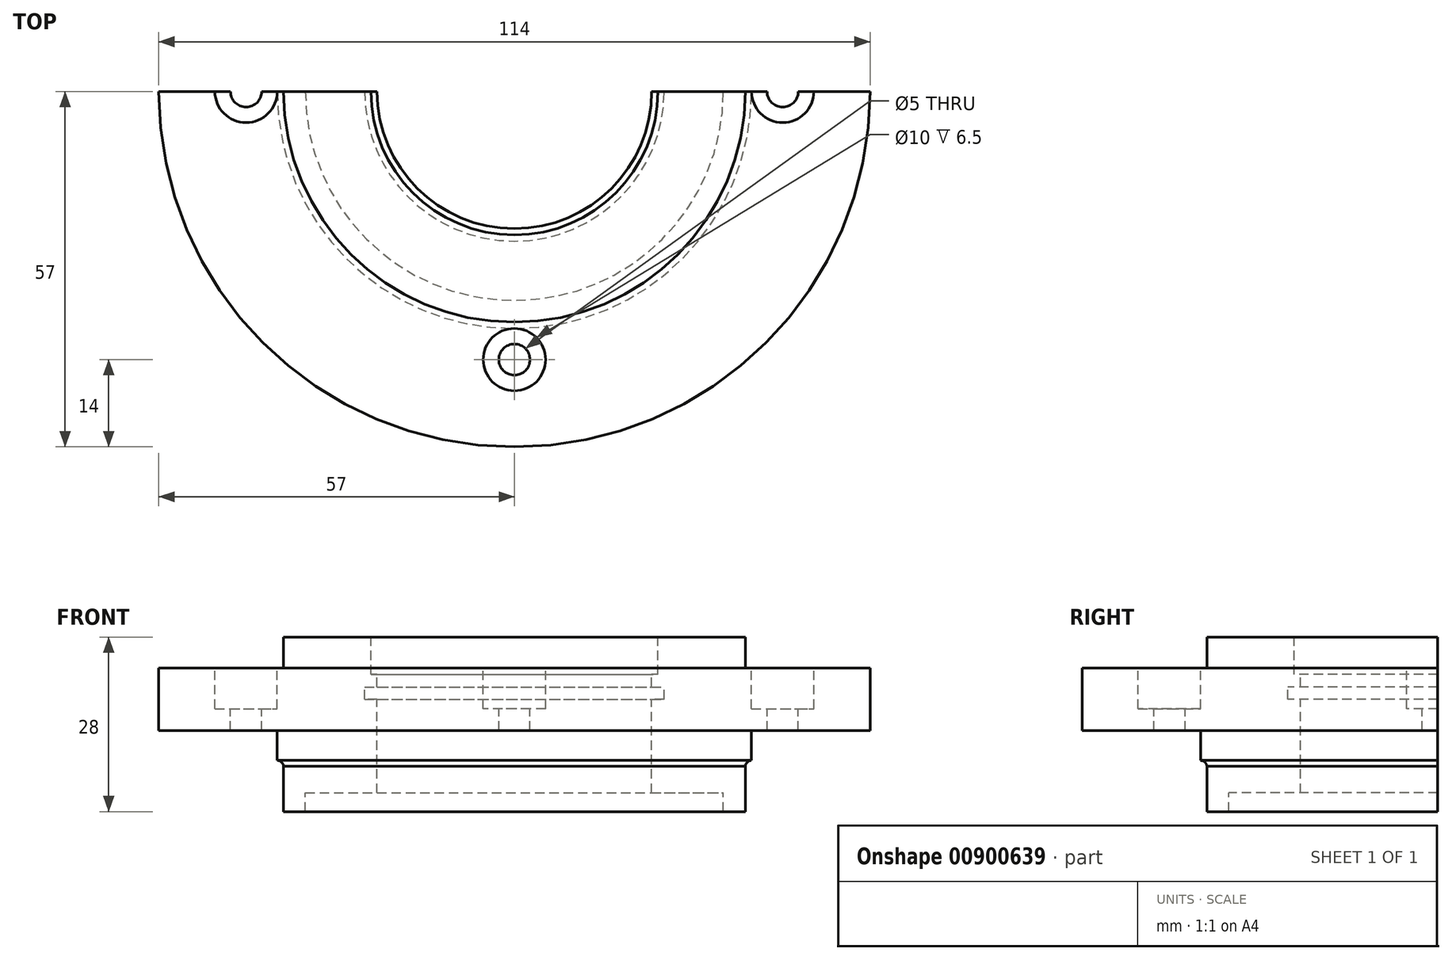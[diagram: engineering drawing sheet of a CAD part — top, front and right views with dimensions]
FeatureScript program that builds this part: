
annotation { "Feature Type Name" : "Feature", "Feature Type Description" : "" }
export const myFeature = defineFeature(function(context is Context, id is Id, definition is map)
    precondition{}
    {
        {
            var Q0;
            Q0=qCreatedBy(makeId("Front.planeOp"),FACE);
            var sketch = newSketch(context, id + "F0", { "sketchPlane" : qUnion([Q0])});
            skLineSegment(sketch, "E0.bottom", {"start": v(5, 21.92) * mm, "end": v(19, 21.92) * mm});
            skLineSegment(sketch, "E0.top", {"start": v(5, -6.08) * mm, "end": v(8.5, -6.08) * mm});
            skLineSegment(sketch, "E0.left", {"start": v(-15, 16.92) * mm, "end": v(-15, 6.92) * mm});
            skLineSegment(sketch, "E0.right", {"start": v(20, 15.92) * mm, "end": v(20, 13.92) * mm});
            skLineSegment(sketch, "E1", {"start": v(5, 21.92) * mm, "end": v(5, 16.92) * mm});
            skLineSegment(sketch, "E2", {"start": v(5, 16.92) * mm, "end": v(-15, 16.92) * mm});
            skLineSegment(sketch, "E3", {"start": v(-15, 6.92) * mm, "end": v(4, 6.92) * mm});
            skLineSegment(sketch, "E4", {"start": v(4, 6.92) * mm, "end": v(4, 2.12) * mm});
            skLineSegment(sketch, "E5", {"start": v(5, 1.2) * mm, "end": v(5, -6.08) * mm});
            skArc(sketch, "E6", {"start": v(5, 1.2) * mm, "mid": v(4.68, 1.86) * mm, "end": v(4, 2.12) * mm});
            skLineSegment(sketch, "E7", {"start": v(19, 21.92) * mm, "end": v(19, 15.92) * mm});
            skLineSegment(sketch, "E8", {"start": v(19, 15.92) * mm, "end": v(20, 15.92) * mm});
            skLineSegment(sketch, "E9", {"start": v(20, 13.92) * mm, "end": v(18, 13.92) * mm});
            skLineSegment(sketch, "E10", {"start": v(18, 13.92) * mm, "end": v(18, 11.92) * mm});
            skLineSegment(sketch, "E11", {"start": v(18, 11.92) * mm, "end": v(20, 11.92) * mm});
            skLineSegment(sketch, "E12.trimOffspring", {"start": v(20, 11.92) * mm, "end": v(20, -3.08) * mm});
            skLineSegment(sketch, "E13", {"start": v(20, -3.08) * mm, "end": v(8.5, -3.08) * mm});
            skLineSegment(sketch, "E14", {"start": v(8.5, -3.08) * mm, "end": v(8.5, -6.08) * mm});
            skLineSegment(sketch, "E15", {"start": v(42, 28.93) * mm, "end": v(42, 3.97) * mm, "construction": true});
            skSolve(sketch);
        }
        {
            var Q0;
            Q0=makeQuery(id+"F0.imprint","IMPRINT",FACE,{"disambiguationData":[TD([[makeQuery(id+"F0.imprint","IMPRINT",EDGE,{"derivedFrom":sQuery(id+"F0.wireOp",EDGE,"E0.bottom")}),-1.0]])]});
            var Q1;
            Q1=sQuery(id+"F0.wireOp",EDGE,"E15");
            revolve(context, id + "F1", {"surfaceOperationType" : NewSurfaceOperationType.NEW, "entities" : qUnion([Q0]), "axis" : qUnion([Q1]), "revolveType" : RevolveType.FULL});
        }
        {
            var Q0;
            Q0=makeQuery(id+"F1.opRevolve","SWEPT_FACE",FACE,{"disambiguationData":[OSD([sQuery(id+"F0.wireOp",EDGE,"E2")])]});
            var sketch = newSketch(context, id + "F2", { "sketchPlane" : qUnion([Q0])});
            skCircle(sketch, "E16", {"center": v(-1, 0) * mm, "radius": 2.5 * mm});
            skCircle(sketch, "E17", {"center": v(42, 0) * mm, "radius": 9.7 * mm, "construction": true});
            skCircle(sketch, "E18", {"center": v(42, 43) * mm, "radius": 2.5 * mm});
            skCircle(sketch, "E19", {"center": v(85, 0) * mm, "radius": 2.5 * mm});
            skCircle(sketch, "E20", {"center": v(42, -43) * mm, "radius": 2.5 * mm});
            skSolve(sketch);
        }
        {
            var Q0;
            Q0=makeQuery(id+"F2.imprint","IMPRINT",FACE,{"disambiguationData":[TD([[makeQuery(id+"F2.imprint","IMPRINT",EDGE,{"derivedFrom":sQuery(id+"F2.wireOp",EDGE,"E16")}),1.0]])]});
            var Q1;
            Q1=makeQuery(id+"F2.imprint","IMPRINT",FACE,{"disambiguationData":[TD([[makeQuery(id+"F2.imprint","IMPRINT",EDGE,{"derivedFrom":sQuery(id+"F2.wireOp",EDGE,"E19")}),1.0]])]});
            var Q2;
            Q2=makeQuery(id+"F2.imprint","IMPRINT",FACE,{"disambiguationData":[TD([[makeQuery(id+"F2.imprint","IMPRINT",EDGE,{"derivedFrom":sQuery(id+"F2.wireOp",EDGE,"E18")}),1.0]])]});
            var Q3;
            Q3=makeQuery(id+"F2.imprint","IMPRINT",FACE,{"disambiguationData":[TD([[makeQuery(id+"F2.imprint","IMPRINT",EDGE,{"derivedFrom":sQuery(id+"F2.wireOp",EDGE,"E20")}),1.0]])]});
            extrude(context, id + "F3", {"entities" : qUnion([Q0, Q1, Q2, Q3]), "operationType" : NewBodyOperationType.REMOVE, "endBound" : BoundingType.THROUGH_ALL, "oppositeDirection" : true, "depth" : 25 * mm, "offsetDistance" : 25 * mm});
        }
        {
            var Q0;
            Q0=makeQuery(id+"F1.opRevolve","SWEPT_FACE",FACE,{"disambiguationData":[OSD([sQuery(id+"F0.wireOp",EDGE,"E2")])]});
            var sketch = newSketch(context, id + "F4", { "sketchPlane" : qUnion([Q0])});
            skCircle(sketch, "E21", {"center": v(-1, 0) * mm, "radius": 5 * mm});
            skCircle(sketch, "E22", {"center": v(42, 43) * mm, "radius": 5 * mm});
            skCircle(sketch, "E23", {"center": v(85, 0) * mm, "radius": 5 * mm});
            skCircle(sketch, "E24", {"center": v(42, -43) * mm, "radius": 5 * mm});
            skSolve(sketch);
        }
        {
            var Q0;
            Q0=makeQuery(id+"F4.imprint","IMPRINT",FACE,{"disambiguationData":[TD([[makeQuery(id+"F4.imprint","IMPRINT",EDGE,{"derivedFrom":sQuery(id+"F4.wireOp",EDGE,"E21")}),1.0]])]});
            var Q1;
            Q1=makeQuery(id+"F4.imprint","IMPRINT",FACE,{"disambiguationData":[TD([[makeQuery(id+"F4.imprint","IMPRINT",EDGE,{"derivedFrom":sQuery(id+"F4.wireOp",EDGE,"E22")}),1.0]])]});
            var Q2;
            Q2=makeQuery(id+"F4.imprint","IMPRINT",FACE,{"disambiguationData":[TD([[makeQuery(id+"F4.imprint","IMPRINT",EDGE,{"derivedFrom":sQuery(id+"F4.wireOp",EDGE,"E23")}),1.0]])]});
            var Q3;
            Q3=makeQuery(id+"F4.imprint","IMPRINT",FACE,{"disambiguationData":[TD([[makeQuery(id+"F4.imprint","IMPRINT",EDGE,{"derivedFrom":sQuery(id+"F4.wireOp",EDGE,"E24")}),1.0]])]});
            extrude(context, id + "F5", {"entities" : qUnion([Q0, Q1, Q2, Q3]), "operationType" : NewBodyOperationType.REMOVE, "oppositeDirection" : true, "depth" : 6.5 * mm, "offsetDistance" : 25 * mm});
        }
        {
            var Q0;
            Q0=qCreatedBy(makeId("Front.planeOp"),FACE);
            var sketch = newSketch(context, id + "F6", { "sketchPlane" : qUnion([Q0])});
            skLineSegment(sketch, "E25.bottom", {"start": v(-37.64, 51.27) * mm, "end": v(99.86, 51.27) * mm});
            skLineSegment(sketch, "E25.top", {"start": v(-37.64, -38.86) * mm, "end": v(99.86, -38.86) * mm});
            skLineSegment(sketch, "E25.left", {"start": v(-37.64, 51.27) * mm, "end": v(-37.64, -38.86) * mm});
            skLineSegment(sketch, "E25.right", {"start": v(99.86, 51.27) * mm, "end": v(99.86, -38.86) * mm});
            skSolve(sketch);
        }
        {
            var Q0;
            Q0=makeQuery(id+"F6.imprint","IMPRINT",FACE,{"disambiguationData":[TD([[makeQuery(id+"F6.imprint","IMPRINT",EDGE,{"derivedFrom":sQuery(id+"F6.wireOp",EDGE,"E25.bottom")}),-1.0]])]});
            extrude(context, id + "F7", {"entities" : qUnion([Q0]), "operationType" : NewBodyOperationType.REMOVE, "endBound" : BoundingType.THROUGH_ALL, "oppositeDirection" : true, "depth" : 25 * mm, "offsetDistance" : 25 * mm});
        }
    });
